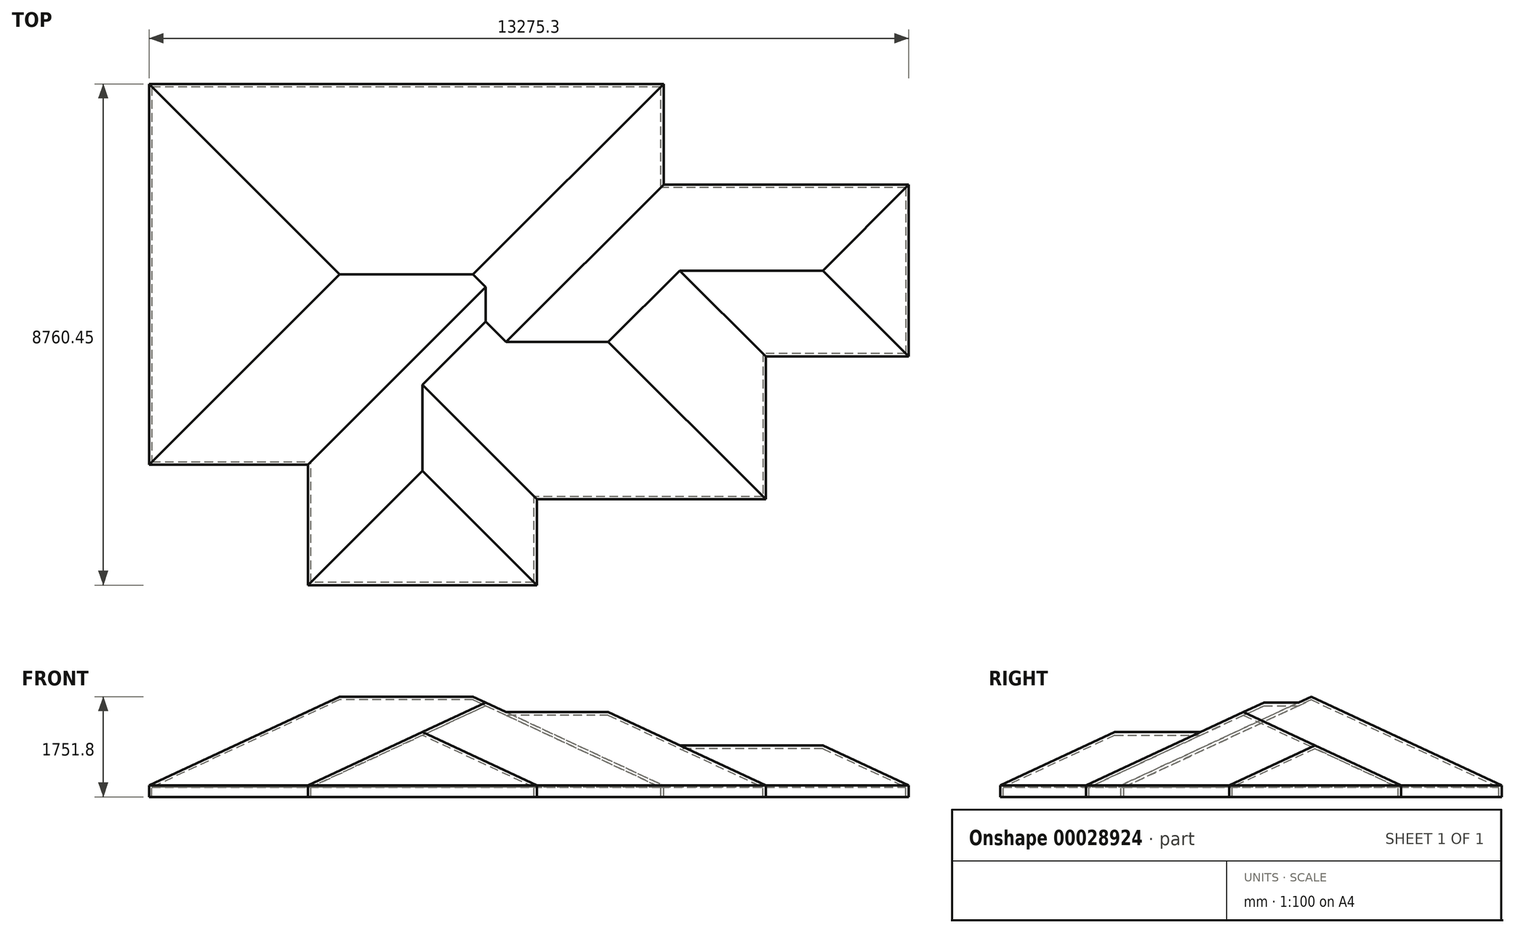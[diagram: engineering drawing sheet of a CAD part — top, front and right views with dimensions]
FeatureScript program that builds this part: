
annotation { "Feature Type Name" : "Feature", "Feature Type Description" : "" }
export const myFeature = defineFeature(function(context is Context, id is Id, definition is map)
    precondition{}
    {
        {
            var Q0;
            Q0=qCreatedBy(makeId("Top.planeOp"),FACE);
            var sketch = newSketch(context, id + "F0", { "sketchPlane" : qUnion([Q0])});
            skLineSegment(sketch, "E0.rect.bottom", {"start": v(3000, 2000) * mm, "end": v(-3000, 2000) * mm});
            skLineSegment(sketch, "E0.rect.top", {"start": v(3000, -2000) * mm, "end": v(-3000, -2000) * mm});
            skLineSegment(sketch, "E0.rect.left", {"start": v(3000, 2000) * mm, "end": v(3000, -2000) * mm});
            skLineSegment(sketch, "E0.rect.right", {"start": v(-3000, 2000) * mm, "end": v(-3000, -2000) * mm});
            skPoint(sketch, "E0.rect.middle", {"position": v(0, 0) * mm});
            skLineSegment(sketch, "E1.rect.bottom", {"start": v(-1000, -3500) * mm, "end": v(-5000, -3500) * mm});
            skLineSegment(sketch, "E1.rect.top", {"start": v(-1000, -500) * mm, "end": v(-5000, -500) * mm});
            skLineSegment(sketch, "E1.rect.left", {"start": v(-1000, -3500) * mm, "end": v(-1000, -500) * mm});
            skLineSegment(sketch, "E1.rect.right", {"start": v(-5000, -3500) * mm, "end": v(-5000, -500) * mm});
            skPoint(sketch, "E1.rect.middle", {"position": v(-3000, -2000) * mm});
            skLineSegment(sketch, "E2.rect.bottom", {"start": v(5500, 3500) * mm, "end": v(500, 3500) * mm});
            skLineSegment(sketch, "E2.rect.top", {"start": v(5500, 500) * mm, "end": v(500, 500) * mm});
            skLineSegment(sketch, "E2.rect.left", {"start": v(5500, 3500) * mm, "end": v(5500, 500) * mm});
            skLineSegment(sketch, "E2.rect.right", {"start": v(500, 3500) * mm, "end": v(500, 500) * mm});
            skPoint(sketch, "E2.rect.middle", {"position": v(3000, 2000) * mm});
            skLineSegment(sketch, "E3", {"start": v(1215.66, 3500) * mm, "end": v(1215.66, 5260.45) * mm});
            skLineSegment(sketch, "E4", {"start": v(1215.66, 5260.45) * mm, "end": v(-7775.33, 5260.45) * mm});
            skLineSegment(sketch, "E5", {"start": v(-7775.33, 5260.45) * mm, "end": v(-7775.33, -1395.22) * mm});
            skLineSegment(sketch, "E6", {"start": v(-7775.33, -1395.22) * mm, "end": v(-5000, -1395.22) * mm});
            skSolve(sketch);
        }
        {
            var Q0;
            {var subQ1=sQuery(id+"F0.wireOp",EDGE,"E3");Q0=makeQuery(id+"F0.imprint","IMPRINT",FACE,{"disambiguationData":[TD([[makeQuery(id+"F0.imprint","IMPRINT",EDGE,{"derivedFrom":subQ1}),1.0]])]});}
            var Q1;
            {var subQ4=sQuery(id+"F0.wireOp",EDGE,"E1.rect.bottom");Q1=makeQuery(id+"F0.imprint","IMPRINT",FACE,{"disambiguationData":[TD([[makeQuery(id+"F0.imprint","IMPRINT",EDGE,{"derivedFrom":subQ4}),-1.0]])]});}
            var Q2;
            {var subQ1=sQuery(id+"F0.wireOp",EDGE,"E0.rect.bottom");var subQ12=sQuery(id+"F0.wireOp",EDGE,"E0.rect.right");var subQ14=makeQuery(id+"F0.imprint","INTERSECT",VERTEX,{"derivedFrom":[subQ1,subQ12]});Q2=makeQuery(id+"F0.imprint","IMPRINT",FACE,{"disambiguationData":[TD([[makeQuery(id+"F0.imprint","IMPRINT",EDGE,{"disambiguationData":[TD([[subQ14,1.0]])],"derivedFrom":subQ1}),1.0]])]});}
            var Q3;
            {var subQ1=sQuery(id+"F0.wireOp",EDGE,"E0.rect.bottom");var subQ5=sQuery(id+"F0.wireOp",EDGE,"E0.rect.left");var subQ7=makeQuery(id+"F0.imprint","INTERSECT",VERTEX,{"derivedFrom":[subQ1,subQ5]});Q3=makeQuery(id+"F0.imprint","IMPRINT",FACE,{"disambiguationData":[TD([[makeQuery(id+"F0.imprint","IMPRINT",EDGE,{"disambiguationData":[TD([[subQ7,-1.0]])],"derivedFrom":subQ1}),1.0]])]});}
            var Q4;
            {var subQ5=sQuery(id+"F0.wireOp",EDGE,"E2.rect.left");Q4=makeQuery(id+"F0.imprint","IMPRINT",FACE,{"disambiguationData":[TD([[makeQuery(id+"F0.imprint","IMPRINT",EDGE,{"derivedFrom":subQ5}),-1.0]])]});}
            var Q5;
            {var subQ1=sQuery(id+"F0.wireOp",EDGE,"E0.rect.right");var subQ5=sQuery(id+"F0.wireOp",EDGE,"E0.rect.top");var subQ6=makeQuery(id+"F0.imprint","INTERSECT",VERTEX,{"derivedFrom":[subQ5,subQ1]});Q5=makeQuery(id+"F0.imprint","IMPRINT",FACE,{"disambiguationData":[TD([[makeQuery(id+"F0.imprint","IMPRINT",EDGE,{"disambiguationData":[TD([[subQ6,1.0]])],"derivedFrom":subQ5}),-1.0]])]});}
            extrude(context, id + "F1", {"entities" : qUnion([Q0, Q1, Q2, Q3, Q4, Q5]), "depth" : 3000 * mm, "hasDraft" : true, "draftAngle" : 65 * degree, "draftPullDirection" : true});
        }
        {
            var Q0;
            Q0=makeQuery(id+"F1.opExtrude","CAP_FACE",FACE,{"disambiguationData":[OSD([sQuery(id+"F0.wireOp",EDGE,"E0.rect.top"),sQuery(id+"F0.wireOp",EDGE,"E0.rect.left"),sQuery(id+"F0.wireOp",EDGE,"E1.rect.bottom"),sQuery(id+"F0.wireOp",EDGE,"E1.rect.left"),sQuery(id+"F0.wireOp",EDGE,"E1.rect.right"),sQuery(id+"F0.wireOp",EDGE,"E2.rect.bottom"),sQuery(id+"F0.wireOp",EDGE,"E2.rect.top"),sQuery(id+"F0.wireOp",EDGE,"E2.rect.left"),sQuery(id+"F0.wireOp",EDGE,"E3"),sQuery(id+"F0.wireOp",EDGE,"E4"),sQuery(id+"F0.wireOp",EDGE,"E5"),sQuery(id+"F0.wireOp",EDGE,"E6")])],"isStart":true});
            extrude(context, id + "F2", {"entities" : qUnion([Q0]), "operationType" : NewBodyOperationType.ADD, "depth" : 200 * mm});
        }
        {
            var Q0;
            Q0=makeQuery(id+"F2.opExtrude","CAP_FACE",FACE,{"disambiguationData":[OSD([sQuery(id+"F0.wireOp",EDGE,"E0.rect.top"),sQuery(id+"F0.wireOp",EDGE,"E0.rect.left"),sQuery(id+"F0.wireOp",EDGE,"E1.rect.bottom"),sQuery(id+"F0.wireOp",EDGE,"E1.rect.left"),sQuery(id+"F0.wireOp",EDGE,"E1.rect.right"),sQuery(id+"F0.wireOp",EDGE,"E2.rect.bottom"),sQuery(id+"F0.wireOp",EDGE,"E2.rect.top"),sQuery(id+"F0.wireOp",EDGE,"E2.rect.left"),sQuery(id+"F0.wireOp",EDGE,"E3"),sQuery(id+"F0.wireOp",EDGE,"E4"),sQuery(id+"F0.wireOp",EDGE,"E5"),sQuery(id+"F0.wireOp",EDGE,"E6")])],"isStart":false});
            shell(context, id + "F3", {"entities" : qUnion([Q0]), "thickness" : 50 * mm});
        }
    });
